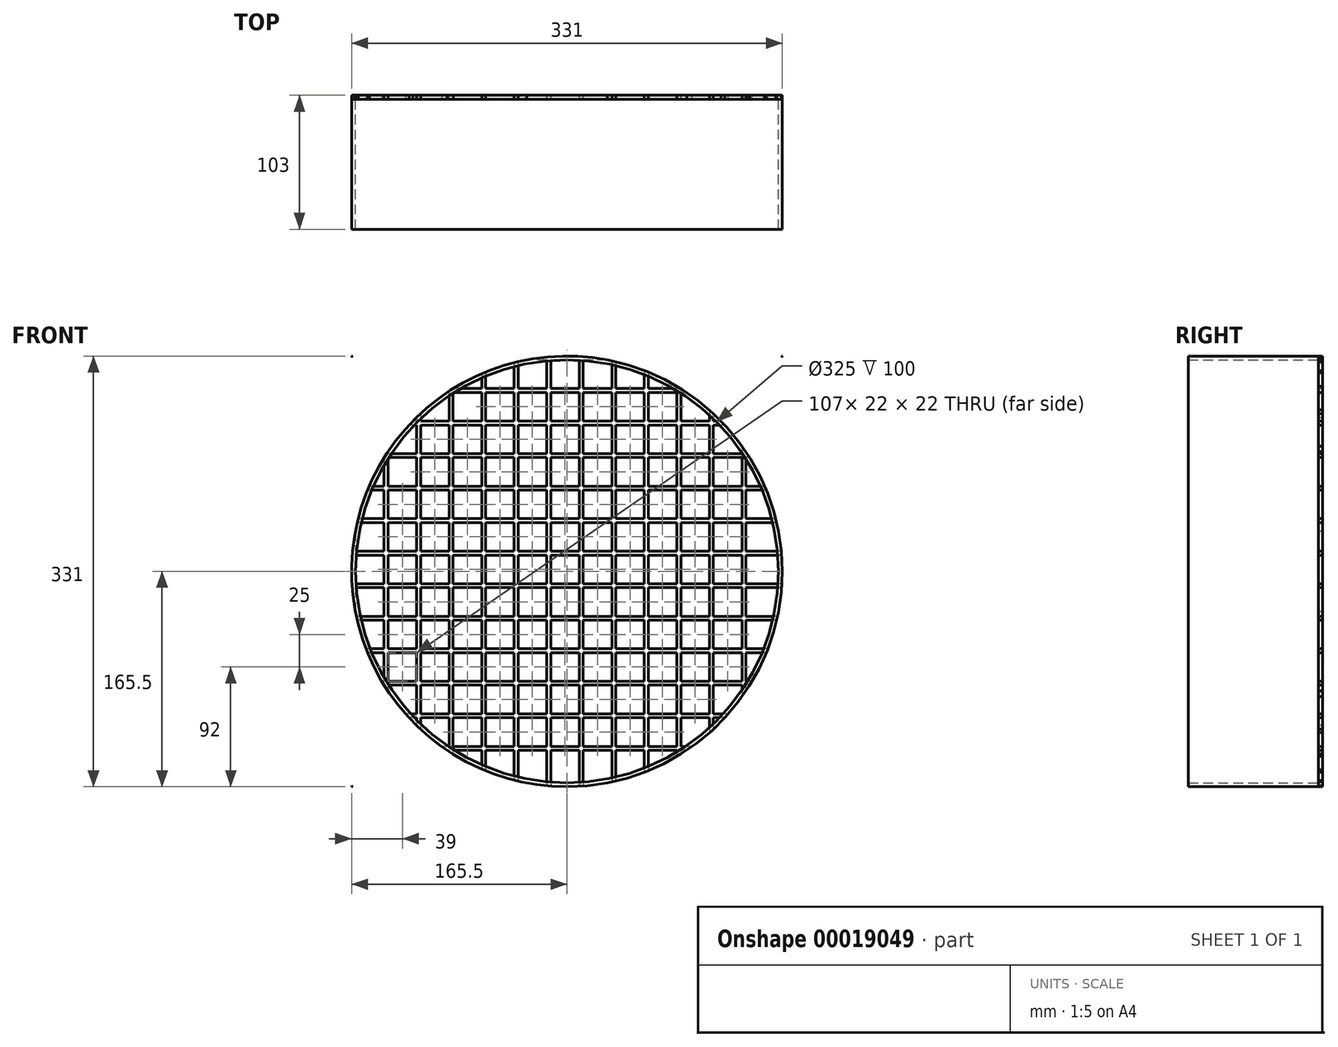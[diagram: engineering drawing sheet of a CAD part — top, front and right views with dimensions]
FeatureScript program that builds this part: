
annotation { "Feature Type Name" : "Feature", "Feature Type Description" : "" }
export const myFeature = defineFeature(function(context is Context, id is Id, definition is map)
    precondition{}
    {
        {
            var Q0;
            Q0=qCreatedBy(makeId("Front.planeOp"),FACE);
            var sketch = newSketch(context, id + "F0", { "sketchPlane" : qUnion([Q0])});
            skCircle(sketch, "E0", {"center": v(0, 0) * mm, "radius": 162.5 * mm});
            skCircle(sketch, "E1", {"center": v(0, 0) * mm, "radius": 165.5 * mm});
            skSolve(sketch);
        }
        {
            var Q0;
            Q0=makeQuery(id+"F0.imprint","IMPRINT",FACE,{"disambiguationData":[TD([[makeQuery(id+"F0.imprint","IMPRINT",EDGE,{"derivedFrom":sQuery(id+"F0.wireOp",EDGE,"E0")}),-1.0]])]});
            extrude(context, id + "F1", {"entities" : qUnion([Q0]), "depth" : 100 * mm});
        }
        {
            var Q0;
            Q0=qCreatedBy(makeId("Front.planeOp"),FACE);
            var sketch = newSketch(context, id + "F2", { "sketchPlane" : qUnion([Q0])});
            skLineSegment(sketch, "E2.bottom", {"start": v(-165.5, 165.5) * mm, "end": v(-162.5, 165.5) * mm});
            skLineSegment(sketch, "E2.top", {"start": v(-165.5, -165.5) * mm, "end": v(-162.5, -165.5) * mm});
            skLineSegment(sketch, "E2.left", {"start": v(-165.5, 165.5) * mm, "end": v(-165.5, -165.5) * mm});
            skLineSegment(sketch, "E2.right", {"start": v(-162.5, 165.5) * mm, "end": v(-162.5, -165.5) * mm});
            skLineSegment(sketch, "E3.1.0.0", {"start": v(-137.5, 165.5) * mm, "end": v(-137.5, -165.5) * mm});
            skLineSegment(sketch, "E3.1.0.1", {"start": v(-140.5, 165.5) * mm, "end": v(-140.5, -165.5) * mm});
            skLineSegment(sketch, "E3.1.0.2", {"start": v(-140.5, -165.5) * mm, "end": v(-137.5, -165.5) * mm});
            skLineSegment(sketch, "E3.1.0.3", {"start": v(-140.5, 165.5) * mm, "end": v(-137.5, 165.5) * mm});
            skLineSegment(sketch, "E3.2.0.0", {"start": v(-112.5, 165.5) * mm, "end": v(-112.5, -165.5) * mm});
            skLineSegment(sketch, "E3.2.0.1", {"start": v(-115.5, 165.5) * mm, "end": v(-115.5, -165.5) * mm});
            skLineSegment(sketch, "E3.2.0.2", {"start": v(-115.5, -165.5) * mm, "end": v(-112.5, -165.5) * mm});
            skLineSegment(sketch, "E3.2.0.3", {"start": v(-115.5, 165.5) * mm, "end": v(-112.5, 165.5) * mm});
            skLineSegment(sketch, "E3.3.0.0", {"start": v(-87.5, 165.5) * mm, "end": v(-87.5, -165.5) * mm});
            skLineSegment(sketch, "E3.3.0.1", {"start": v(-90.5, 165.5) * mm, "end": v(-90.5, -165.5) * mm});
            skLineSegment(sketch, "E3.3.0.2", {"start": v(-90.5, -165.5) * mm, "end": v(-87.5, -165.5) * mm});
            skLineSegment(sketch, "E3.3.0.3", {"start": v(-90.5, 165.5) * mm, "end": v(-87.5, 165.5) * mm});
            skLineSegment(sketch, "E3.4.0.0", {"start": v(-62.5, 165.5) * mm, "end": v(-62.5, -165.5) * mm});
            skLineSegment(sketch, "E3.4.0.1", {"start": v(-65.5, 165.5) * mm, "end": v(-65.5, -165.5) * mm});
            skLineSegment(sketch, "E3.4.0.2", {"start": v(-65.5, -165.5) * mm, "end": v(-62.5, -165.5) * mm});
            skLineSegment(sketch, "E3.4.0.3", {"start": v(-65.5, 165.5) * mm, "end": v(-62.5, 165.5) * mm});
            skLineSegment(sketch, "E3.5.0.0", {"start": v(-37.5, 165.5) * mm, "end": v(-37.5, -165.5) * mm});
            skLineSegment(sketch, "E3.5.0.1", {"start": v(-40.5, 165.5) * mm, "end": v(-40.5, -165.5) * mm});
            skLineSegment(sketch, "E3.5.0.2", {"start": v(-40.5, -165.5) * mm, "end": v(-37.5, -165.5) * mm});
            skLineSegment(sketch, "E3.5.0.3", {"start": v(-40.5, 165.5) * mm, "end": v(-37.5, 165.5) * mm});
            skLineSegment(sketch, "E3.6.0.0", {"start": v(-12.5, 165.5) * mm, "end": v(-12.5, -165.5) * mm});
            skLineSegment(sketch, "E3.6.0.1", {"start": v(-15.5, 165.5) * mm, "end": v(-15.5, -165.5) * mm});
            skLineSegment(sketch, "E3.6.0.2", {"start": v(-15.5, -165.5) * mm, "end": v(-12.5, -165.5) * mm});
            skLineSegment(sketch, "E3.6.0.3", {"start": v(-15.5, 165.5) * mm, "end": v(-12.5, 165.5) * mm});
            skLineSegment(sketch, "E3.7.0.0", {"start": v(12.5, 165.5) * mm, "end": v(12.5, -165.5) * mm});
            skLineSegment(sketch, "E3.7.0.1", {"start": v(9.5, 165.5) * mm, "end": v(9.5, -165.5) * mm});
            skLineSegment(sketch, "E3.7.0.2", {"start": v(9.5, -165.5) * mm, "end": v(12.5, -165.5) * mm});
            skLineSegment(sketch, "E3.7.0.3", {"start": v(9.5, 165.5) * mm, "end": v(12.5, 165.5) * mm});
            skLineSegment(sketch, "E3.8.0.0", {"start": v(37.5, 165.5) * mm, "end": v(37.5, -165.5) * mm});
            skLineSegment(sketch, "E3.8.0.1", {"start": v(34.5, 165.5) * mm, "end": v(34.5, -165.5) * mm});
            skLineSegment(sketch, "E3.8.0.2", {"start": v(34.5, -165.5) * mm, "end": v(37.5, -165.5) * mm});
            skLineSegment(sketch, "E3.8.0.3", {"start": v(34.5, 165.5) * mm, "end": v(37.5, 165.5) * mm});
            skLineSegment(sketch, "E3.9.0.0", {"start": v(62.5, 165.5) * mm, "end": v(62.5, -165.5) * mm});
            skLineSegment(sketch, "E3.9.0.1", {"start": v(59.5, 165.5) * mm, "end": v(59.5, -165.5) * mm});
            skLineSegment(sketch, "E3.9.0.2", {"start": v(59.5, -165.5) * mm, "end": v(62.5, -165.5) * mm});
            skLineSegment(sketch, "E3.9.0.3", {"start": v(59.5, 165.5) * mm, "end": v(62.5, 165.5) * mm});
            skLineSegment(sketch, "E3.10.0.0", {"start": v(87.5, 165.5) * mm, "end": v(87.5, -165.5) * mm});
            skLineSegment(sketch, "E3.10.0.1", {"start": v(84.5, 165.5) * mm, "end": v(84.5, -165.5) * mm});
            skLineSegment(sketch, "E3.10.0.2", {"start": v(84.5, -165.5) * mm, "end": v(87.5, -165.5) * mm});
            skLineSegment(sketch, "E3.10.0.3", {"start": v(84.5, 165.5) * mm, "end": v(87.5, 165.5) * mm});
            skLineSegment(sketch, "E3.11.0.0", {"start": v(112.5, 165.5) * mm, "end": v(112.5, -165.5) * mm});
            skLineSegment(sketch, "E3.11.0.1", {"start": v(109.5, 165.5) * mm, "end": v(109.5, -165.5) * mm});
            skLineSegment(sketch, "E3.11.0.2", {"start": v(109.5, -165.5) * mm, "end": v(112.5, -165.5) * mm});
            skLineSegment(sketch, "E3.11.0.3", {"start": v(109.5, 165.5) * mm, "end": v(112.5, 165.5) * mm});
            skLineSegment(sketch, "E3.12.0.0", {"start": v(137.5, 165.5) * mm, "end": v(137.5, -165.5) * mm});
            skLineSegment(sketch, "E3.12.0.1", {"start": v(134.5, 165.5) * mm, "end": v(134.5, -165.5) * mm});
            skLineSegment(sketch, "E3.12.0.2", {"start": v(134.5, -165.5) * mm, "end": v(137.5, -165.5) * mm});
            skLineSegment(sketch, "E3.12.0.3", {"start": v(134.5, 165.5) * mm, "end": v(137.5, 165.5) * mm});
            skLineSegment(sketch, "E3.direction1", {"start": v(-162.5, -165.5) * mm, "end": v(-137.5, -165.5) * mm, "construction": true});
            skSolve(sketch);
        }
        {
            var Q0;
            Q0 = qSketchRegion(id + "F2", true);
            extrude(context, id + "F3", {"entities" : qUnion([Q0]), "operationType" : NewBodyOperationType.ADD, "oppositeDirection" : true, "depth" : 3 * mm});
        }
        {
            var Q0;
            Q0=qCreatedBy(makeId("Front.planeOp"),FACE);
            var sketch = newSketch(context, id + "F4", { "sketchPlane" : qUnion([Q0])});
            skLineSegment(sketch, "E4.bottom", {"start": v(165.5, 165.5) * mm, "end": v(-165.5, 165.5) * mm});
            skLineSegment(sketch, "E4.top", {"start": v(165.5, 162.5) * mm, "end": v(-165.5, 162.5) * mm});
            skLineSegment(sketch, "E4.left", {"start": v(165.5, 165.5) * mm, "end": v(165.5, 162.5) * mm});
            skLineSegment(sketch, "E4.right", {"start": v(-165.5, 165.5) * mm, "end": v(-165.5, 162.5) * mm});
            skLineSegment(sketch, "E5.1.0.0", {"start": v(165.5, 140.5) * mm, "end": v(-165.5, 140.5) * mm});
            skLineSegment(sketch, "E5.1.0.1", {"start": v(165.5, 137.5) * mm, "end": v(-165.5, 137.5) * mm});
            skLineSegment(sketch, "E5.1.0.2", {"start": v(165.5, 140.5) * mm, "end": v(165.5, 137.5) * mm});
            skLineSegment(sketch, "E5.1.0.3", {"start": v(-165.5, 140.5) * mm, "end": v(-165.5, 137.5) * mm});
            skLineSegment(sketch, "E5.2.0.0", {"start": v(165.5, 115.5) * mm, "end": v(-165.5, 115.5) * mm});
            skLineSegment(sketch, "E5.2.0.1", {"start": v(165.5, 112.5) * mm, "end": v(-165.5, 112.5) * mm});
            skLineSegment(sketch, "E5.2.0.2", {"start": v(165.5, 115.5) * mm, "end": v(165.5, 112.5) * mm});
            skLineSegment(sketch, "E5.2.0.3", {"start": v(-165.5, 115.5) * mm, "end": v(-165.5, 112.5) * mm});
            skLineSegment(sketch, "E5.3.0.0", {"start": v(165.5, 90.5) * mm, "end": v(-165.5, 90.5) * mm});
            skLineSegment(sketch, "E5.3.0.1", {"start": v(165.5, 87.5) * mm, "end": v(-165.5, 87.5) * mm});
            skLineSegment(sketch, "E5.3.0.2", {"start": v(165.5, 90.5) * mm, "end": v(165.5, 87.5) * mm});
            skLineSegment(sketch, "E5.3.0.3", {"start": v(-165.5, 90.5) * mm, "end": v(-165.5, 87.5) * mm});
            skLineSegment(sketch, "E5.4.0.0", {"start": v(165.5, 65.5) * mm, "end": v(-165.5, 65.5) * mm});
            skLineSegment(sketch, "E5.4.0.1", {"start": v(165.5, 62.5) * mm, "end": v(-165.5, 62.5) * mm});
            skLineSegment(sketch, "E5.4.0.2", {"start": v(165.5, 65.5) * mm, "end": v(165.5, 62.5) * mm});
            skLineSegment(sketch, "E5.4.0.3", {"start": v(-165.5, 65.5) * mm, "end": v(-165.5, 62.5) * mm});
            skLineSegment(sketch, "E5.5.0.0", {"start": v(165.5, 40.5) * mm, "end": v(-165.5, 40.5) * mm});
            skLineSegment(sketch, "E5.5.0.1", {"start": v(165.5, 37.5) * mm, "end": v(-165.5, 37.5) * mm});
            skLineSegment(sketch, "E5.5.0.2", {"start": v(165.5, 40.5) * mm, "end": v(165.5, 37.5) * mm});
            skLineSegment(sketch, "E5.5.0.3", {"start": v(-165.5, 40.5) * mm, "end": v(-165.5, 37.5) * mm});
            skLineSegment(sketch, "E5.6.0.0", {"start": v(165.5, 15.5) * mm, "end": v(-165.5, 15.5) * mm});
            skLineSegment(sketch, "E5.6.0.1", {"start": v(165.5, 12.5) * mm, "end": v(-165.5, 12.5) * mm});
            skLineSegment(sketch, "E5.6.0.2", {"start": v(165.5, 15.5) * mm, "end": v(165.5, 12.5) * mm});
            skLineSegment(sketch, "E5.6.0.3", {"start": v(-165.5, 15.5) * mm, "end": v(-165.5, 12.5) * mm});
            skLineSegment(sketch, "E5.7.0.0", {"start": v(165.5, -9.5) * mm, "end": v(-165.5, -9.5) * mm});
            skLineSegment(sketch, "E5.7.0.1", {"start": v(165.5, -12.5) * mm, "end": v(-165.5, -12.5) * mm});
            skLineSegment(sketch, "E5.7.0.2", {"start": v(165.5, -9.5) * mm, "end": v(165.5, -12.5) * mm});
            skLineSegment(sketch, "E5.7.0.3", {"start": v(-165.5, -9.5) * mm, "end": v(-165.5, -12.5) * mm});
            skLineSegment(sketch, "E5.8.0.0", {"start": v(165.5, -34.5) * mm, "end": v(-165.5, -34.5) * mm});
            skLineSegment(sketch, "E5.8.0.1", {"start": v(165.5, -37.5) * mm, "end": v(-165.5, -37.5) * mm});
            skLineSegment(sketch, "E5.8.0.2", {"start": v(165.5, -34.5) * mm, "end": v(165.5, -37.5) * mm});
            skLineSegment(sketch, "E5.8.0.3", {"start": v(-165.5, -34.5) * mm, "end": v(-165.5, -37.5) * mm});
            skLineSegment(sketch, "E5.9.0.0", {"start": v(165.5, -59.5) * mm, "end": v(-165.5, -59.5) * mm});
            skLineSegment(sketch, "E5.9.0.1", {"start": v(165.5, -62.5) * mm, "end": v(-165.5, -62.5) * mm});
            skLineSegment(sketch, "E5.9.0.2", {"start": v(165.5, -59.5) * mm, "end": v(165.5, -62.5) * mm});
            skLineSegment(sketch, "E5.9.0.3", {"start": v(-165.5, -59.5) * mm, "end": v(-165.5, -62.5) * mm});
            skLineSegment(sketch, "E5.10.0.0", {"start": v(165.5, -84.5) * mm, "end": v(-165.5, -84.5) * mm});
            skLineSegment(sketch, "E5.10.0.1", {"start": v(165.5, -87.5) * mm, "end": v(-165.5, -87.5) * mm});
            skLineSegment(sketch, "E5.10.0.2", {"start": v(165.5, -84.5) * mm, "end": v(165.5, -87.5) * mm});
            skLineSegment(sketch, "E5.10.0.3", {"start": v(-165.5, -84.5) * mm, "end": v(-165.5, -87.5) * mm});
            skLineSegment(sketch, "E5.11.0.0", {"start": v(165.5, -109.5) * mm, "end": v(-165.5, -109.5) * mm});
            skLineSegment(sketch, "E5.11.0.1", {"start": v(165.5, -112.5) * mm, "end": v(-165.5, -112.5) * mm});
            skLineSegment(sketch, "E5.11.0.2", {"start": v(165.5, -109.5) * mm, "end": v(165.5, -112.5) * mm});
            skLineSegment(sketch, "E5.11.0.3", {"start": v(-165.5, -109.5) * mm, "end": v(-165.5, -112.5) * mm});
            skLineSegment(sketch, "E5.12.0.0", {"start": v(165.5, -134.5) * mm, "end": v(-165.5, -134.5) * mm});
            skLineSegment(sketch, "E5.12.0.1", {"start": v(165.5, -137.5) * mm, "end": v(-165.5, -137.5) * mm});
            skLineSegment(sketch, "E5.12.0.2", {"start": v(165.5, -134.5) * mm, "end": v(165.5, -137.5) * mm});
            skLineSegment(sketch, "E5.12.0.3", {"start": v(-165.5, -134.5) * mm, "end": v(-165.5, -137.5) * mm});
            skLineSegment(sketch, "E5.direction1", {"start": v(-165.5, 165.5) * mm, "end": v(-165.5, 140.5) * mm, "construction": true});
            skSolve(sketch);
        }
        {
            var Q0;
            Q0 = qSketchRegion(id + "F4", true);
            extrude(context, id + "F5", {"entities" : qUnion([Q0]), "operationType" : NewBodyOperationType.ADD, "oppositeDirection" : true, "depth" : 3 * mm});
        }
        {
            var Q0;
            Q0=qCreatedBy(makeId("Front.planeOp"),FACE);
            var sketch = newSketch(context, id + "F6", { "sketchPlane" : qUnion([Q0])});
            skCircle(sketch, "E6", {"center": v(0, 0) * mm, "radius": 165.5 * mm});
            skCircle(sketch, "E7", {"center": v(0, 0) * mm, "radius": 233.52 * mm});
            skSolve(sketch);
        }
        {
            var Q0;
            Q0 = qSketchRegion(id + "F6", true);
            extrude(context, id + "F7", {"entities" : qUnion([Q0]), "operationType" : NewBodyOperationType.REMOVE, "oppositeDirection" : true, "depth" : 25 * mm, "hasDraft" : true, "draftAngle" : 3 * degree});
        }
    });
